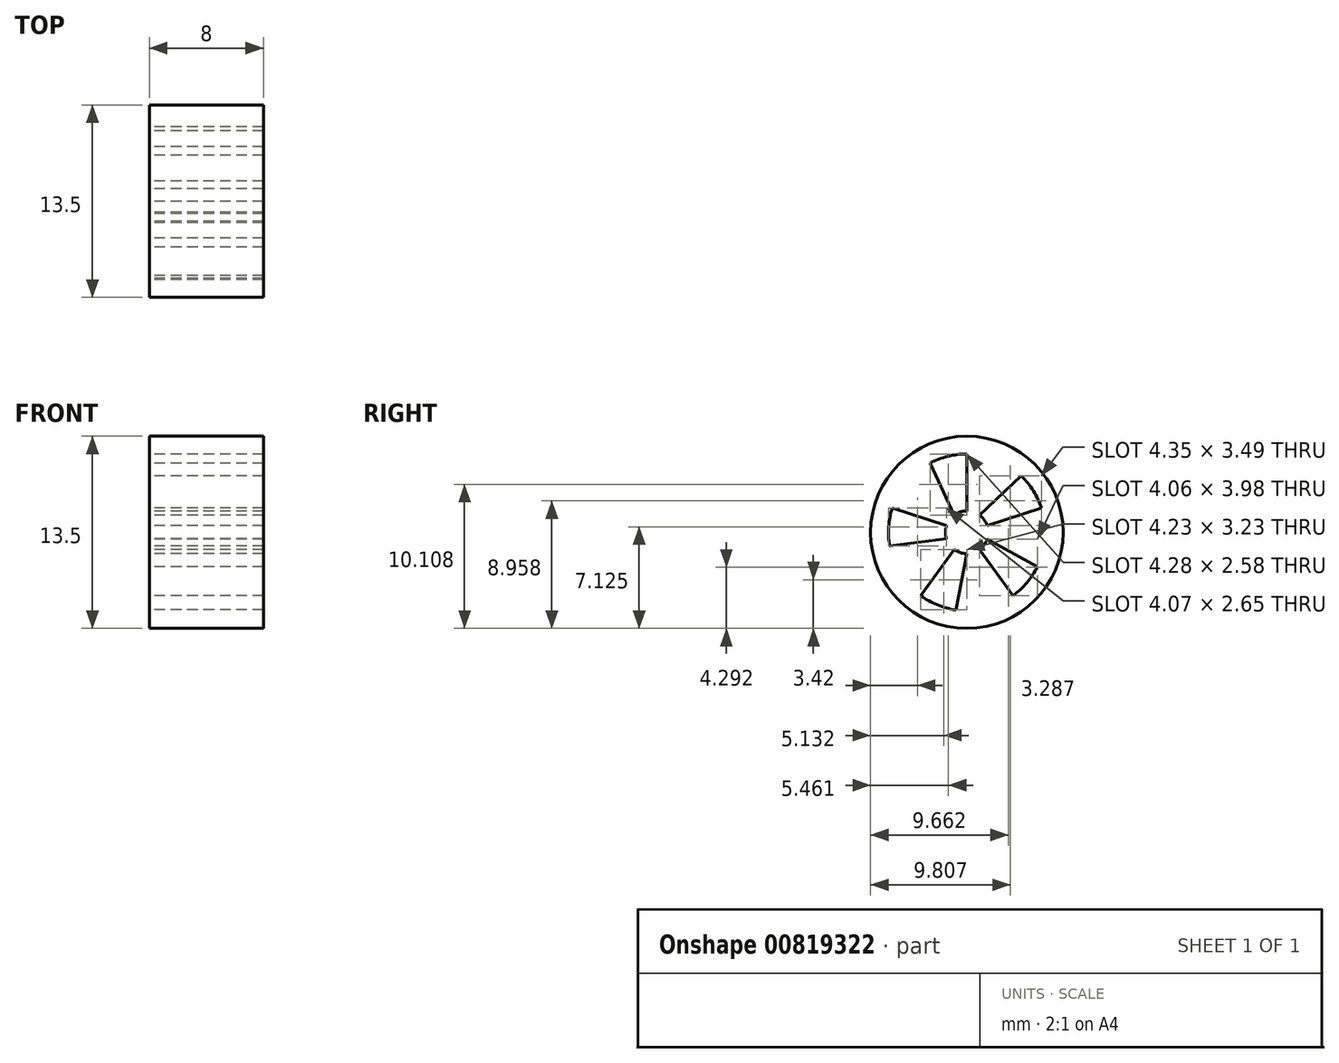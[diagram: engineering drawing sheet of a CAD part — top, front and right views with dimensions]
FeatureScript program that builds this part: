
annotation { "Feature Type Name" : "Feature", "Feature Type Description" : "" }
export const myFeature = defineFeature(function(context is Context, id is Id, definition is map)
    precondition{}
    {
        {
            var Q0;
            Q0=qCreatedBy(makeId("Right.planeOp"),FACE);
            var sketch = newSketch(context, id + "F0", { "sketchPlane" : qUnion([Q0])});
            skCircle(sketch, "E0", {"center": v(0, 0) * mm, "radius": 6.75 * mm});
            skSolve(sketch);
        }
        {
            var Q0;
            Q0=makeQuery(id+"F0.imprint","IMPRINT",FACE,{"disambiguationData":[TD([[makeQuery(id+"F0.imprint","IMPRINT",EDGE,{"derivedFrom":sQuery(id+"F0.wireOp",EDGE,"E0")}),1.0]])]});
            extrude(context, id + "F1", {"entities" : qUnion([Q0]), "depth" : 8 * mm, "offsetDistance" : 25 * mm});
        }
        {
            var Q0;
            Q0=makeQuery(id+"F1.opExtrude","CAP_FACE",FACE,{"disambiguationData":[OSD([sQuery(id+"F0.wireOp",EDGE,"E0")])],"isStart":true});
            var sketch = newSketch(context, id + "F2", { "sketchPlane" : qUnion([Q0])});
            skCircle(sketch, "E1", {"center": v(0, 0) * mm, "radius": 1.5 * mm});
            skCircle(sketch, "E2", {"center": v(0, 0) * mm, "radius": 5.5 * mm});
            skLineSegment(sketch, "E3", {"start": v(0, 1.5) * mm, "end": v(0, 5.5) * mm});
            skLineSegment(sketch, "E4", {"start": v(0.88, 1.22) * mm, "end": v(2.58, 4.86) * mm});
            skLineSegment(sketch, "E5.1.0", {"start": v(-1.43, 0.46) * mm, "end": v(-5.23, 1.7) * mm});
            skLineSegment(sketch, "E5.1.1", {"start": v(-0.88, 1.21) * mm, "end": v(-3.82, 3.95) * mm});
            skLineSegment(sketch, "E5.2.0", {"start": v(-0.88, -1.21) * mm, "end": v(-3.23, -4.45) * mm});
            skLineSegment(sketch, "E5.2.1", {"start": v(-1.43, -0.47) * mm, "end": v(-4.94, -2.42) * mm});
            skLineSegment(sketch, "E5.3.0", {"start": v(0.88, -1.21) * mm, "end": v(3.23, -4.45) * mm});
            skLineSegment(sketch, "E5.3.1", {"start": v(0, -1.5) * mm, "end": v(0.77, -5.45) * mm});
            skLineSegment(sketch, "E5.4.0", {"start": v(1.43, 0.46) * mm, "end": v(5.23, 1.7) * mm});
            skLineSegment(sketch, "E5.4.1", {"start": v(1.43, -0.46) * mm, "end": v(5.42, -0.95) * mm});
            skSolve(sketch);
        }
        {
            var Q0;
            {var subQ0=sQuery(id+"F2.wireOp",EDGE,"E5.1.0");Q0=makeQuery(id+"F2.imprint","IMPRINT",FACE,{"disambiguationData":[TD([[makeQuery(id+"F2.imprint","IMPRINT",EDGE,{"derivedFrom":subQ0}),-1.0]])]});}
            var Q1;
            {var subQ0=sQuery(id+"F2.wireOp",EDGE,"E3");Q1=makeQuery(id+"F2.imprint","IMPRINT",FACE,{"disambiguationData":[TD([[makeQuery(id+"F2.imprint","IMPRINT",EDGE,{"derivedFrom":subQ0}),-1.0]])]});}
            var Q2;
            {var subQ0=sQuery(id+"F2.wireOp",EDGE,"E5.4.0");Q2=makeQuery(id+"F2.imprint","IMPRINT",FACE,{"disambiguationData":[TD([[makeQuery(id+"F2.imprint","IMPRINT",EDGE,{"derivedFrom":subQ0}),-1.0]])]});}
            var Q3;
            {var subQ0=sQuery(id+"F2.wireOp",EDGE,"E5.3.0");Q3=makeQuery(id+"F2.imprint","IMPRINT",FACE,{"disambiguationData":[TD([[makeQuery(id+"F2.imprint","IMPRINT",EDGE,{"derivedFrom":subQ0}),-1.0]])]});}
            var Q4;
            {var subQ0=sQuery(id+"F2.wireOp",EDGE,"E5.2.0");Q4=makeQuery(id+"F2.imprint","IMPRINT",FACE,{"disambiguationData":[TD([[makeQuery(id+"F2.imprint","IMPRINT",EDGE,{"derivedFrom":subQ0}),-1.0]])]});}
            extrude(context, id + "F3", {"entities" : qUnion([Q0, Q1, Q2, Q3, Q4]), "operationType" : NewBodyOperationType.REMOVE, "oppositeDirection" : true, "depth" : 8 * mm, "offsetDistance" : 25 * mm});
        }
    });
